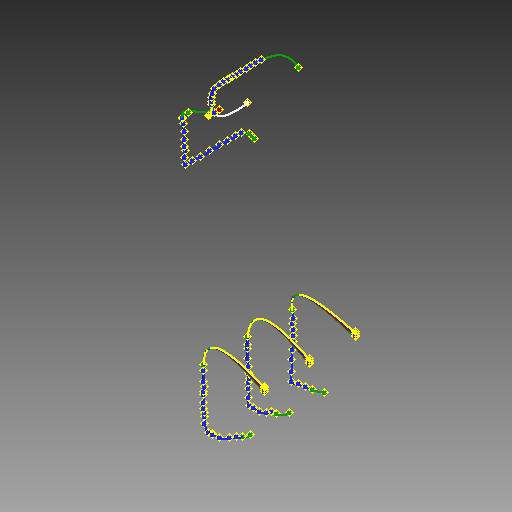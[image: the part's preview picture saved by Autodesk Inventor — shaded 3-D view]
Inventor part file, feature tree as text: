
AUTODESK INVENTOR PART (.ipt)
format: ipt  version: 2017 (Build 210142000, 142)  size: 718,848 bytes
history: native  units: mm (DEFAULTED — no unit token found)
features: other x150, plane x8, sketch x8, sweep x8
ambient origin geometry x8: Origin, YZ Plane, XZ Plane, XY Plane, X Axis, Y Axis, Z Axis, Center Point
bodies: Body1 (feature_tree), Body2 (feature_tree), Body3 (feature_tree), Body4 (feature_tree), Body5 (feature_tree), Body6 (feature_tree), Body7 (feature_tree), Body8 (feature_tree)
feature tree (174):
  other  "Work Point1"
  other  "Work Point2"
  other  "Wire1"
  other  "Work Point3"
  other  "Work Point4"
  other  "Wire2"
  other  "Work Point5"
  other  "Work Point6"
  other  "Wire3"
  other  "Work Point7"
  other  "Work Point8"
  other  "Wire4"
  other  "Work Point9"
  other  "Work Point10"
  other  "Wire5"
  other  "Work Point11"
  other  "Work Point12"
  other  "Wire6"
  other  "Work Point13"
  other  "Work Point14"
  other  "Wire7"
  other  "Work Point15"
  other  "Work Point16"
  other  "Wire8"
  other  "Work Point17"
  other  "Work Point18"
  other  "Wire9"
  other  "Work Point19"
  other  "Work Point20"
  other  "Wire10"
  other  "Work Point21"
  other  "Work Point22"
  other  "Wire11"
  other  "Work Point23"
  other  "Work Point24"
  other  "Wire12"
  other  "Work Point25"
  other  "Work Point26"
  other  "Wire13"
  other  "Work Point27"
  other  "Work Point28"
  other  "Wire14"
  other  "Work Point29"
  other  "Work Point30"
  other  "Wire15"
  other  "Work Point31"
  other  "Work Point32"
  other  "Wire16"
  other  "Work Point33"
  other  "Work Point34"
  other  "Wire17"
  other  "Work Point35"
  other  "Work Point36"
  other  "Wire18"
  other  "Work Point61"
  other  "Work Point62"
  other  "Segment1"
  other  "Work Point63"
  other  "Work Point64"
  other  "Work Point65"
  other  "Work Point66"
  other  "Work Point67"
  other  "Work Point68"
  other  "Work Point69"
  other  "Work Point70"
  other  "Work Point71"
  other  "Work Point72"
  other  "Segment2"
  other  "Work Point73"
  other  "Work Point74"
  other  "Work Point75"
  other  "Work Point76"
  plane  "Work Plane19"
  plane  "Work Plane20"
  other  "Work Point77"
  other  "Work Point78"
  other  "Segment3"
  other  "Work Point79"
  other  "Work Point80"
  other  "Work Point81"
  other  "Work Point82"
  other  "Work Point83"
  other  "Work Point84"
  other  "Work Point85"
  other  "Work Point86"
  other  "Work Point87"
  other  "Work Point88"
  other  "Work Point89"
  other  "Work Point90"
  other  "Work Point91"
  other  "Work Point92"
  plane  "Work Plane21"
  other  "Work Point93"
  other  "Work Point94"
  other  "Segment4"
  other  "Work Point95"
  other  "Work Point96"
  other  "Work Point97"
  other  "Work Point98"
  other  "Work Point99"
  other  "Work Point100"
  other  "Work Point101"
  other  "Work Point102"
  other  "Work Point103"
  other  "Work Point104"
  other  "Work Point105"
  other  "Work Point106"
  other  "Work Point107"
  other  "Segment5"
  other  "Work Point108"
  other  "Segment6"
  other  "Work Point109"
  other  "Work Point110"
  plane  "Work Plane22"
  other  "Work Point111"
  other  "Work Point112"
  other  "Segment7"
  other  "Work Point113"
  other  "Work Point114"
  other  "Work Point115"
  other  "Work Point116"
  other  "Work Point117"
  other  "Work Point118"
  other  "Work Point119"
  other  "Work Point120"
  other  "Work Point121"
  other  "Work Point122"
  other  "Work Point123"
  other  "Work Point124"
  other  "Work Point125"
  other  "Work Point126"
  other  "Work Point127"
  plane  "Work Plane23"
  other  "Work Point128"
  other  "Work Point129"
  other  "Segment8"
  other  "Work Point130"
  other  "Work Point131"
  other  "Work Point132"
  other  "Work Point133"
  other  "Work Point134"
  other  "Work Point135"
  other  "Work Point136"
  other  "Work Point137"
  other  "Work Point138"
  other  "Work Point139"
  other  "Work Point140"
  plane  "Work Plane24"
  plane  "Work Plane25"
  plane  "Work Plane26"
  sketch  "Sketch19"  dims[d36=0.0mm d37=0.0mm d38=0.0mm d39=0.0mm]
  other  "Srf19"
  sketch  "Sketch20"  dims[d40=0.0mm d41=0.0mm d42=0.0mm d43=0.0mm]
  other  "Srf20"
  sketch  "Sketch21"  dims[d44=0.0mm d45=0.0mm d46=0.0mm d47=0.0mm]
  other  "Srf21"
  sketch  "Sketch22"  dims[d48=0.0mm d49=0.0mm d50=0.0mm d51=0.0mm]
  other  "Srf22"
  sketch  "Sketch23"
  other  "Srf23"
  sketch  "Sketch24"
  other  "Srf24"
  sketch  "Sketch25"
  other  "Srf25"
  sketch  "Sketch26"
  other  "Srf26"
  sweep  "SweepSrf19"
  sweep  "SweepSrf20"
  sweep  "SweepSrf21"
  sweep  "SweepSrf22"
  sweep  "SweepSrf23"
  sweep  "SweepSrf24"
  sweep  "SweepSrf25"
  sweep  "SweepSrf26"
